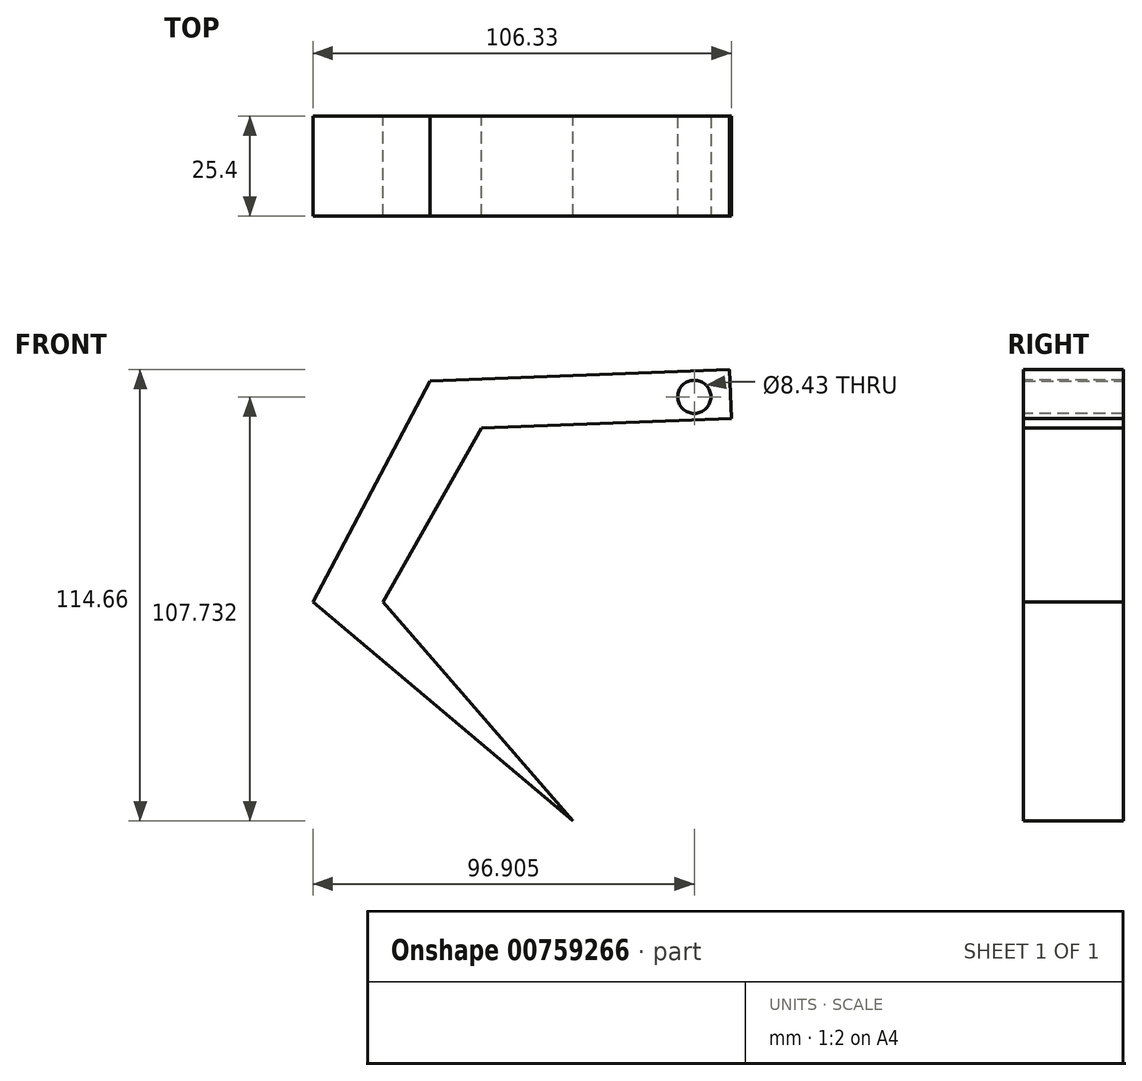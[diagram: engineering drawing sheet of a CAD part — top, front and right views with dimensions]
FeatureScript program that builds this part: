
annotation { "Feature Type Name" : "Feature", "Feature Type Description" : "" }
export const myFeature = defineFeature(function(context is Context, id is Id, definition is map)
    precondition{}
    {
        {
            var Q0;
            Q0=qCreatedBy(makeId("Front.planeOp"),FACE);
            var sketch = newSketch(context, id + "F0", { "sketchPlane" : qUnion([Q0])});
            skLineSegment(sketch, "E0", {"start": v(39.82, 35.95) * mm, "end": v(-36.33, 33.05) * mm});
            skLineSegment(sketch, "E1", {"start": v(39.82, 35.95) * mm, "end": v(40.3, 23.51) * mm});
            skLineSegment(sketch, "E2", {"start": v(40.3, 23.51) * mm, "end": v(-23.16, 21.1) * mm});
            skLineSegment(sketch, "E3", {"start": v(-23.16, 21.1) * mm, "end": v(-36.33, 33.05) * mm});
            skLineSegment(sketch, "E4", {"start": v(-36.33, 33.05) * mm, "end": v(-66.04, -23.07) * mm});
            skLineSegment(sketch, "E5", {"start": v(-23.16, 21.1) * mm, "end": v(-48.26, -23.07) * mm});
            skLineSegment(sketch, "E6", {"start": v(-48.26, -23.07) * mm, "end": v(-66.04, -23.07) * mm});
            skLineSegment(sketch, "E7", {"start": v(-48.26, -23.07) * mm, "end": v(0, -78.71) * mm});
            skLineSegment(sketch, "E8", {"start": v(-66.04, -23.07) * mm, "end": v(0, -78.71) * mm});
            skSolve(sketch);
        }
        {
            var Q0;
            Q0=makeQuery(id+"F0.imprint","IMPRINT",FACE,{"disambiguationData":[TD([[makeQuery(id+"F0.imprint","IMPRINT",EDGE,{"derivedFrom":sQuery(id+"F0.wireOp",EDGE,"E0")}),1.0]])]});
            var Q1;
            Q1=makeQuery(id+"F0.imprint","IMPRINT",FACE,{"disambiguationData":[TD([[makeQuery(id+"F0.imprint","IMPRINT",EDGE,{"derivedFrom":sQuery(id+"F0.wireOp",EDGE,"E3")}),1.0]])]});
            var Q2;
            Q2=makeQuery(id+"F0.imprint","IMPRINT",FACE,{"disambiguationData":[TD([[makeQuery(id+"F0.imprint","IMPRINT",EDGE,{"derivedFrom":sQuery(id+"F0.wireOp",EDGE,"E6")}),1.0]])]});
            extrude(context, id + "F1", {"entities" : qUnion([Q0, Q1, Q2]), "depth" : 25.4 * mm, "offsetDistance" : 25.4 * mm});
        }
        {
            var Q0;
            Q0=makeQuery(id+"F1.opExtrude","CAP_FACE",FACE,{"disambiguationData":[OSD([sQuery(id+"F0.wireOp",EDGE,"E0"),sQuery(id+"F0.wireOp",EDGE,"E1"),sQuery(id+"F0.wireOp",EDGE,"E2"),sQuery(id+"F0.wireOp",EDGE,"E4"),sQuery(id+"F0.wireOp",EDGE,"E5"),sQuery(id+"F0.wireOp",EDGE,"E7"),sQuery(id+"F0.wireOp",EDGE,"E8")])],"isStart":false});
            var sketch = newSketch(context, id + "F2", { "sketchPlane" : qUnion([Q0])});
            skCircle(sketch, "E9", {"center": v(30.86, 29.02) * mm, "radius": 4.22 * mm});
            skSolve(sketch);
        }
        {
            var Q0;
            Q0=makeQuery(id+"F2.imprint","IMPRINT",FACE,{"disambiguationData":[TD([[makeQuery(id+"F2.imprint","IMPRINT",EDGE,{"derivedFrom":sQuery(id+"F2.wireOp",EDGE,"E9")}),1.0]])]});
            extrude(context, id + "F3", {"entities" : qUnion([Q0]), "operationType" : NewBodyOperationType.REMOVE, "oppositeDirection" : true, "depth" : 25.4 * mm, "offsetDistance" : 25.4 * mm});
        }
    });
